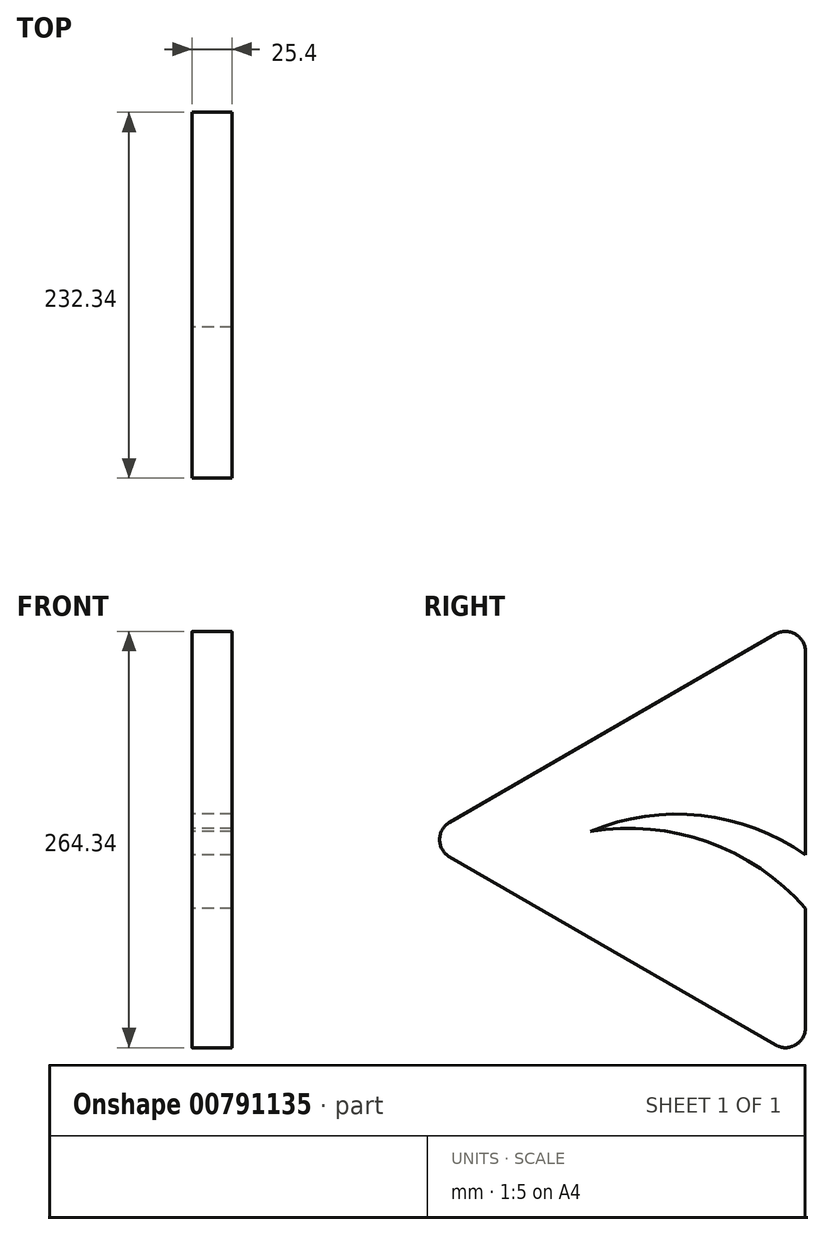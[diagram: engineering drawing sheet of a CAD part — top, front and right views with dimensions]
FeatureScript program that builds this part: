
annotation { "Feature Type Name" : "Feature", "Feature Type Description" : "" }
export const myFeature = defineFeature(function(context is Context, id is Id, definition is map)
    precondition{}
    {
        {
            var Q0;
            Q0=qCreatedBy(makeId("Right.planeOp"),FACE);
            var sketch = newSketch(context, id + "F0", { "sketchPlane" : qUnion([Q0])});
            skCircle(sketch, "E0.cCircle", {"center": v(-349.34, 0) * mm, "radius": 163.36 * mm, "construction": true});
            skLineSegment(sketch, "E0.0", {"start": v(-493.65, 11) * mm, "end": v(-286.71, 130.47) * mm});
            skLineSegment(sketch, "E0.1", {"start": v(-267.66, 119.47) * mm, "end": v(-267.66, -119.47) * mm});
            skLineSegment(sketch, "E0.2", {"start": v(-286.71, -130.47) * mm, "end": v(-493.65, -11) * mm});
            skLineSegment(sketch, "E1", {"start": v(-10.8, 0) * mm, "end": v(-192.14, 172.25) * mm, "construction": true});
            skLineSegment(sketch, "E2", {"start": v(-192.14, 172.25) * mm, "end": v(-349.34, 0) * mm, "construction": true});
            skPoint(sketch, "E3.visualSharp", {"position": v(-267.66, 141.47) * mm});
            skArc(sketch, "E3.filletArc", {"start": v(-267.66, 119.47) * mm, "mid": v(-274.01, 130.47) * mm, "end": v(-286.71, 130.47) * mm});
            skPoint(sketch, "E4.visualSharp", {"position": v(-512.7, 0) * mm});
            skArc(sketch, "E4.filletArc", {"start": v(-493.65, 11) * mm, "mid": v(-500, 0) * mm, "end": v(-493.65, -11) * mm});
            skPoint(sketch, "E5.visualSharp", {"position": v(-267.66, -141.47) * mm});
            skArc(sketch, "E5.filletArc", {"start": v(-286.71, -130.47) * mm, "mid": v(-274.01, -130.47) * mm, "end": v(-267.66, -119.47) * mm});
            skArc(sketch, "E6", {"start": v(-404.25, 5.15) * mm, "mid": v(-329.67, -1.57) * mm, "end": v(-267.66, -43.57) * mm});
            skArc(sketch, "E7", {"start": v(-404.25, 5.15) * mm, "mid": v(-334.03, 15.35) * mm, "end": v(-267.66, -9.78) * mm});
            skPoint(sketch, "E8", {"position": v(-267.66, -9.78) * mm});
            skSolve(sketch);
        }
        {
            var Q0;
            Q0=makeQuery(id+"F0.imprint","IMPRINT",FACE,{"disambiguationData":[TD([[makeQuery(id+"F0.imprint","IMPRINT",EDGE,{"derivedFrom":sQuery(id+"F0.wireOp",EDGE,"E0.0")}),-1.0]])]});
            extrude(context, id + "F1", {"entities" : qUnion([Q0]), "depth" : 25.4 * mm, "offsetDistance" : 25.4 * mm});
        }
    });
